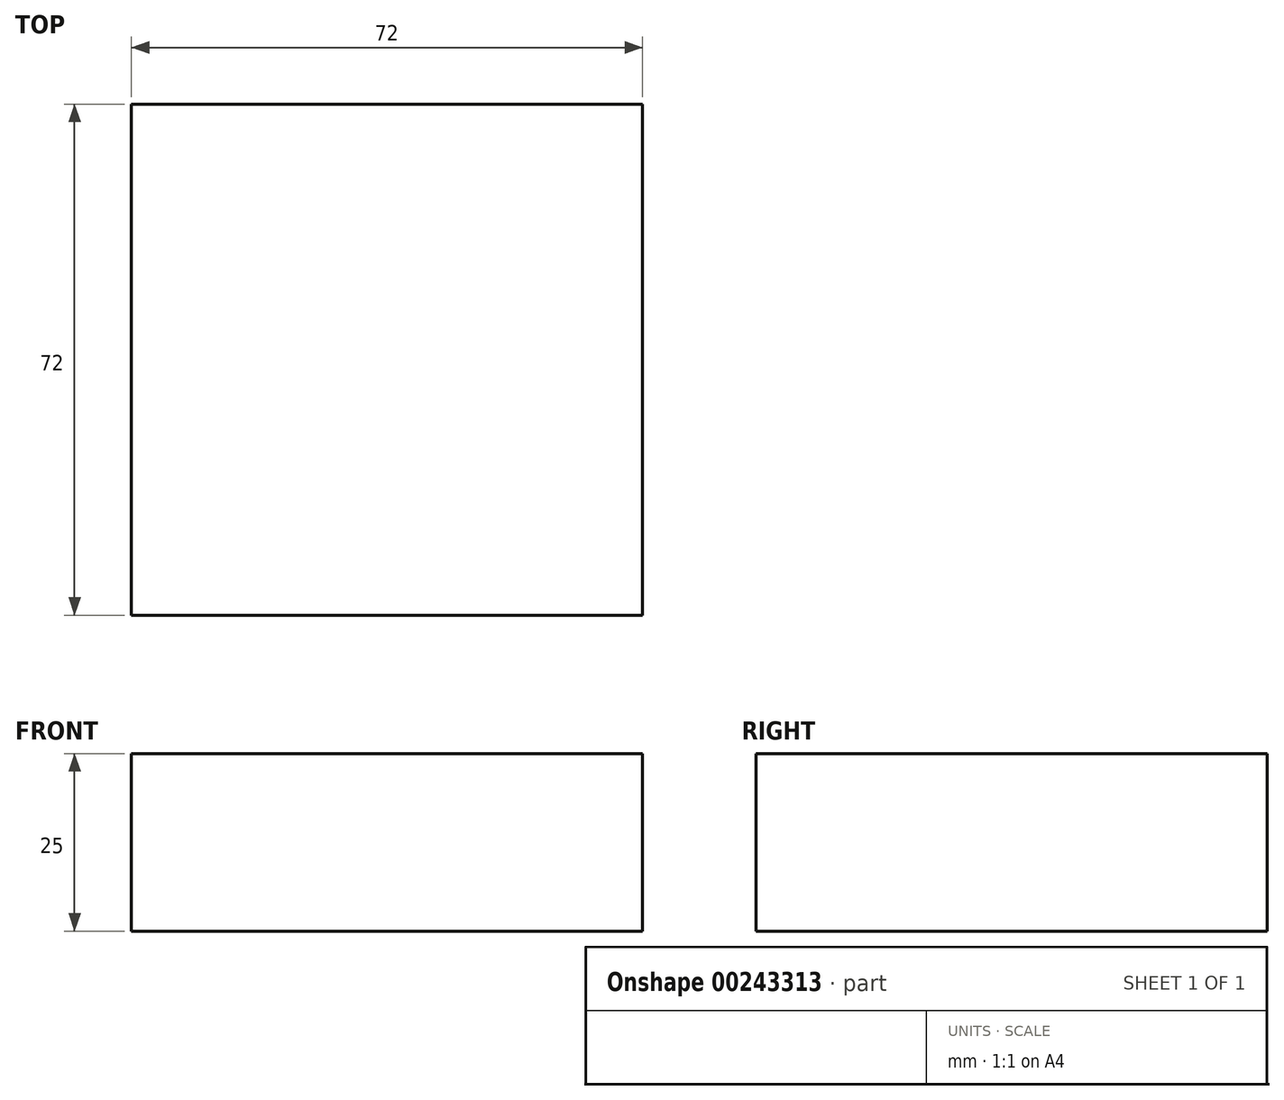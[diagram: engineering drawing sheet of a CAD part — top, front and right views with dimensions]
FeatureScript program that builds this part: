
annotation { "Feature Type Name" : "Feature", "Feature Type Description" : "" }
export const myFeature = defineFeature(function(context is Context, id is Id, definition is map)
    precondition{}
    {
        {
            var Q0;
            Q0=qCreatedBy(makeId("Top.planeOp"),FACE);
            var sketch = newSketch(context, id + "F0", { "sketchPlane" : qUnion([Q0])});
            skLineSegment(sketch, "E0.bottom", {"start": v(-36, 36) * mm, "end": v(36, 36) * mm});
            skLineSegment(sketch, "E0.top", {"start": v(-36, -36) * mm, "end": v(36, -36) * mm});
            skLineSegment(sketch, "E0.left", {"start": v(-36, 36) * mm, "end": v(-36, -36) * mm});
            skLineSegment(sketch, "E0.right", {"start": v(36, 36) * mm, "end": v(36, -36) * mm});
            skPoint(sketch, "E0.middle", {"position": v(0, 0) * mm});
            skSolve(sketch);
        }
        {
            var Q0;
            Q0 = qSketchRegion(id + "F0", true);
            extrude(context, id + "F1", {"entities" : qUnion([Q0]), "depth" : 25 * mm});
        }
    });
